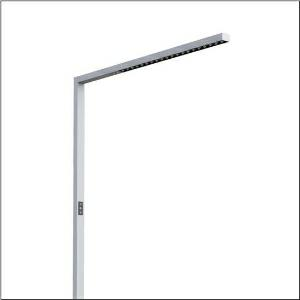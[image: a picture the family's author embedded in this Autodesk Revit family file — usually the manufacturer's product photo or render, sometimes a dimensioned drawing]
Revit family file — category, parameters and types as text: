
# Revit family: silica_r__31_floor_51my52fatcs_4ab2
name_source: partatom
category: Lighting Fixtures
units: mm (PartAtom-declared; Revit-internal decimal feet)

## family parameters
Cut with Voids When Loaded = No
Host = Face
Light Source = No
Part Type = Normal
Room Calculation Point = No
Round Connector Dimension = Use Diameter
Shared = No

## types (1)
- --- (1 x LED, 8520 lm, 71 W, 4000K)
    Apparent Load = 71 VA
    CIE Flux Codes = 86 100 100 24 100
    Color Rendering = 80
    Color Temperature = 4000K
    Default Elevation = 1800 mm
    Description = Silica® 31 Floor, floorstanding luminaire, secondary optical cover: cover panel, of PMMA, light emission: direct/indirect distribution, primary light characteristic: symmetric, installation type: not mounted, LED, rated luminous flux: 8.520lm, luminous efficacy: 120lm/W, light colour: 8tw, colour temperature: 2700..6500K, control gear: Touchdim, daylight-dependent control, with cable with plug, mains connection: 230V, AC, 50Hz, connection cable pre-assembled, rated input power: 71W, luminaire head, of aluminium, metallic grey (RAL 9006), length: 1.203mm, width: 52mm, supporting column, angular, of aluminium, metallic grey (RAL 9006), baseplate, of steel, metallic grey (RAL 9006), protection rating (complete): IP20, insulation class (complete): insulation class I (protective earthing), certification: CE, permissible operating ambient temperature: -20..+40°C, standard: EN 50419, packaging unit: 1 piece
    Height = 36 mm
    Lamp = 1 x LED
    Lamp Light Flux = 8520 lm
    Lamp Power = 71 W
    Lamp count = 1
    Length = 1203 mm
    Luminous efficacy = 120 lm/W
    Manufacturer = Siteco
    ModVariant = No
    Model = 51MY52FATCS
    Mounting Place = Floor
    Mounting Type = Freestanding
    Number of Poles = 1
    OnlyDefault = Yes
    Power Factor = 1
    Product Name = Silica® 31 Floor
    Product group = floorstanding luminaire
    ProductGroupID = 1302
    Protection Class = Protection class I
    Protection Degree = IP 20
    RLX_Detail_Level = 1
    RLX_Emergency_Light_Flux = 0 lm
    RLX_Emergency_Type = 0
    RLX_Emergency_Type_DB = No
    RlxData = <blob elided: 19573 chars, md5=afd63235>
    Socket = socket
    Standby Power = 0 W
    System Light Flux = 8520 lm
    System Power = 71 W
    Type Comments = factory setting
    Type Image = l_1275303.jpg
    URL = http://relux.com
    VarID = @adj_080212
    Voltage = 0 V
    Weight = 0.00 kg
    Width = 52 mm  [stored 0.170604 ft]

note: [stored X ft] marks values corroborated as IEEE doubles in the binary element streams (Revit-internal decimal feet)

## geometry (parser evidence)
native form markers: Blend x4, Sweep x16
no freeform markers — native parametric forms only
